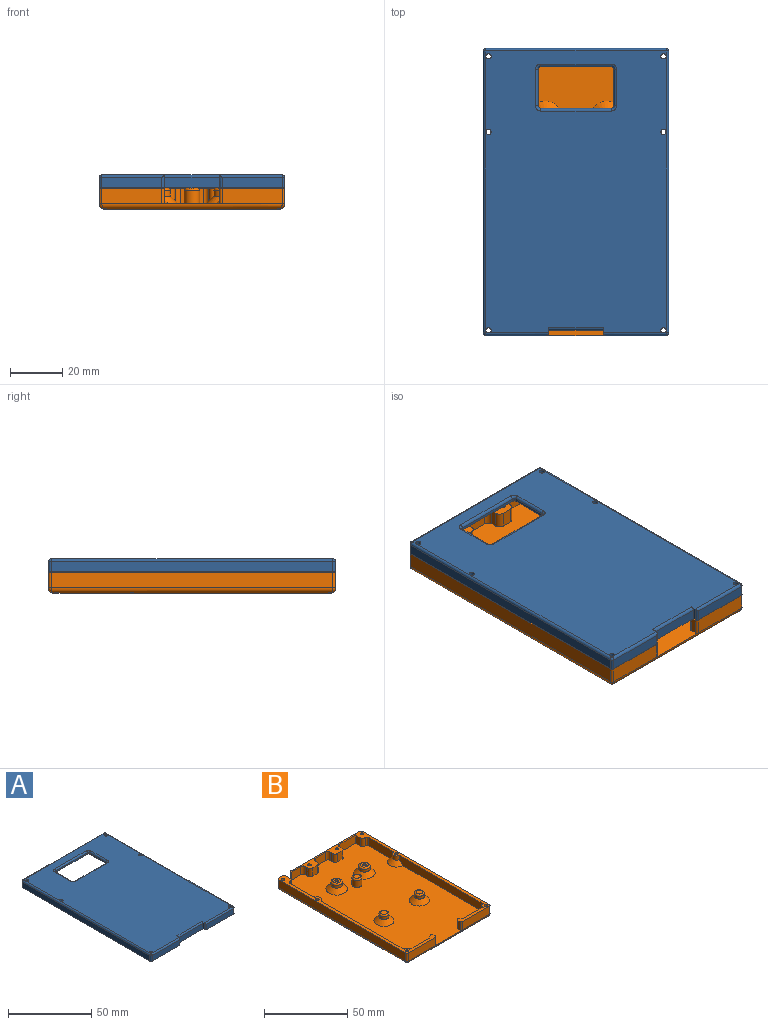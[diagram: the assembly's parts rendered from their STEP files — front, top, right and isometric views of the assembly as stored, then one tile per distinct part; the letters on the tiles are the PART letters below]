
ASSEMBLY  parts=2 mates=1
PART A: 99 faces, bbox 71x110x5 mm
  f0: plane 4x3.68mm, normal (0,1,0), area 14.7mm2, adj f49,f76,f80,f81
  f1: plane 108x69mm, normal (0,0,1), area 6836.2mm2, adj f5,f7,f15,f16,f17,f18,f19,f22
  f2: plane 1x1mm, normal (0,0,1), area 0.2mm2, adj f15,f68,f74
  f3: plane 1x1mm, normal (0,0,1), area 0.2mm2, adj f16,f69,f75
  f4: plane 107x67mm, normal (0,0,-1), area 6312.3mm2, adj f12,f13,f14,f21,f23,f24,f25,f26
  f5: plane 5x2mm, normal (1,0,0), area 5.2mm2, adj f1,f6,f49,f66,f94
  f6: plane 21x4mm, normal (0,-1,0), area 84mm2, adj f5,f7,f49,f94
  f7: plane 5x2mm, normal (-1,0,0), area 5.2mm2, adj f1,f6,f49,f65,f94
  f8: plane 23x4mm, normal (0,-1,0), area 92mm2, adj f49,f65,f67,f68
  f9: plane 108x4mm, normal (1,0,0), area 432mm2, adj f49,f67,f73,f74
  f10: plane 58.32x4mm, normal (0,1,0), area 233.3mm2, adj f49,f73,f79,f80
  f11: plane 108x4mm, normal (-1,0,0), area 432mm2, adj f49,f70,f75,f76
  f12: plane 27x1mm, normal (0,1,0), area 27mm2, adj f4,f52,f53,f54
  f13: plane 14x1mm, normal (1,0,0), area 14mm2, adj f4,f52,f57,f58
  f14: plane 27x1mm, normal (0,-1,0), area 27mm2, adj f4,f57,f60,f63
  f15: cylinder r=1mm len=5mm, axis (0,0,-1), area 31.4mm2, adj f1,f2,f49
  f16: cylinder r=1mm len=5mm, axis (0,0,-1), area 31.4mm2, adj f1,f3,f49
  f17: cylinder r=1mm len=5mm, axis (0,0,-1), area 31.4mm2, adj f1,f49
  f18: cylinder r=1mm len=5mm, axis (0,0,-1), area 31.4mm2, adj f1,f49
  f19: cylinder r=1mm len=5mm, axis (0,0,-1), area 31.4mm2, adj f1,f49
  f20: plane 23x4mm, normal (0,-1,0), area 92mm2, adj f49,f66,f69,f70
  f21: plane 14x1mm, normal (-1,0,0), area 14mm2, adj f4,f54,f59,f60
  f22: cylinder r=1mm len=5mm, axis (0,0,-1), area 31.4mm2, adj f1,f49
  f23: plane 53.71x3mm, normal (0,-1,0), area 161.1mm2, adj f4,f49,f79,f92
  f24: plane 4x3mm, normal (-1,0,0), area 12mm2, adj f4,f49,f92,f93
  f25: plane 3x2.61mm, normal (0,-1,0), area 7.8mm2, adj f4,f26,f49,f93
  f26: plane 22.5x3mm, normal (-1,0,0), area 65.5mm2, adj f4,f25,f27,f49,f96
  f27: cylinder r=2.5mm len=5mm, axis (0,0,1), area 7.9mm2, adj f26,f28,f49,f96
  f28: plane 33x3mm, normal (-1,0,0), area 97mm2, adj f4,f27,f49,f84,f96
  f29: plane 14.38x3mm, normal (0,1,0), area 43.1mm2, adj f4,f49,f84,f85
  f30: cylinder r=3mm len=6mm, axis (0,0,1), area 44.4mm2, adj f4,f49,f85,f86
  f31: plane 14.38x3mm, normal (0,-1,0), area 43.1mm2, adj f4,f49,f86,f87
  f32: plane 33x3mm, normal (-1,0,0), area 97mm2, adj f4,f33,f49,f87,f98
  f33: cylinder r=2.5mm len=2.5mm, axis (0,0,1), area 3.9mm2, adj f32,f34,f49,f98
  f34: plane 16.5x3mm, normal (0,1,0), area 47.5mm2, adj f4,f33,f35,f49,f98
  f35: plane 3.73x3mm, normal (0.6,0.8,0), area 14mm2, adj f4,f34,f49,f82
  f36: plane 20.33x3mm, normal (0,1,0), area 61mm2, adj f4,f49,f82,f83
  f37: plane 3.73x3mm, normal (-0.6,0.8,0), area 14mm2, adj f4,f38,f49,f83
  f38: plane 16.5x3mm, normal (0,1,0), area 47.5mm2, adj f4,f37,f39,f49,f97
  f39: cylinder r=2.5mm len=2.5mm, axis (0,0,1), area 3.9mm2, adj f38,f40,f49,f97
  f40: plane 33x3mm, normal (1,0,0), area 97mm2, adj f4,f39,f49,f91,f97
  f41: plane 14.38x3mm, normal (0,-1,0), area 43.1mm2, adj f4,f49,f88,f91
  f42: cylinder r=3mm len=6mm, axis (0,0,1), area 44.4mm2, adj f4,f49,f88,f89
  f43: plane 14.38x3mm, normal (0,1,0), area 43.1mm2, adj f4,f49,f89,f90
  f44: plane 33x3mm, normal (1,0,0), area 97mm2, adj f4,f45,f49,f90,f95
  f45: cylinder r=2.5mm len=5mm, axis (0,0,1), area 7.9mm2, adj f44,f46,f49,f95
  f46: plane 22.5x3mm, normal (1,0,0), area 65.5mm2, adj f4,f45,f47,f49,f95
  f47: plane 3x2.68mm, normal (0,-1,0), area 8mm2, adj f4,f46,f49,f64
  f48: plane 5x3mm, normal (1,0,0), area 15mm2, adj f4,f49,f64,f81
  f49: plane 110x71mm, normal (0,0,-1), area 872.7mm2, adj f0,f5,f6,f7,f8,f9,f10,f11
  f50: cylinder r=3mm len=6mm, axis (0,0,1), area 56.5mm2, adj f4,f51
  f51: plane 6x6mm, normal (0,0,-1), area 28.3mm2, adj f50
  f52: cylinder r=1mm len=1mm, axis (0,0,1), area 1.6mm2, adj f4,f12,f13,f55
  f53: cylinder r=1mm len=27mm, axis (1,0,0), area 42.4mm2, adj f1,f12,f55,f56
  f54: cylinder r=1mm len=1mm, axis (0,0,-1), area 1.6mm2, adj f4,f12,f21,f56
  f55: torus R=2mm, axis (0,0,1), area 3.4mm2, adj f1,f52,f53,f58
  f56: torus R=2mm, axis (0,0,1), area 3.4mm2, adj f1,f53,f54,f59
  f57: cylinder r=1mm len=1mm, axis (0,0,-1), area 1.6mm2, adj f4,f13,f14,f61
  f58: cylinder r=1mm len=14mm, axis (0,-1,0), area 22mm2, adj f1,f13,f55,f61
  f59: cylinder r=1mm len=14mm, axis (0,1,0), area 22mm2, adj f1,f21,f56,f62
  f60: cylinder r=1mm len=1mm, axis (0,0,1), area 1.6mm2, adj f4,f14,f21,f62
  f61: torus R=2mm, axis (0,0,1), area 3.4mm2, adj f1,f57,f58,f63
  f62: torus R=2mm, axis (0,0,1), area 3.4mm2, adj f1,f59,f60,f63
  f63: cylinder r=1mm len=27mm, axis (-1,0,0), area 42.4mm2, adj f1,f14,f61,f62
  f64: cylinder r=1mm len=3mm, axis (0,0,1), area 4.7mm2, adj f4,f47,f48,f49
  f65: cylinder r=1mm len=5mm, axis (0,0,1), area 7.3mm2, adj f7,f8,f49,f68
  f66: cylinder r=1mm len=5mm, axis (0,0,-1), area 7.3mm2, adj f5,f20,f49,f69
  f67: cylinder r=1mm len=4mm, axis (0,0,1), area 6.3mm2, adj f8,f9,f49,f71
  f68: cylinder r=1mm len=24mm, axis (-1,0,0), area 37.1mm2, adj f1,f2,f8,f65,f71
  f69: cylinder r=1mm len=24mm, axis (-1,0,0), area 37.1mm2, adj f1,f3,f20,f66,f72
  f70: cylinder r=1mm len=4mm, axis (0,0,-1), area 6.3mm2, adj f11,f20,f49,f72
  f71: sphere r=1mm, area 1.6mm2, adj f67,f68,f74
  f72: sphere r=1mm, area 1.6mm2, adj f69,f70,f75
  f73: cylinder r=1mm len=4mm, axis (0,0,1), area 6.3mm2, adj f9,f10,f49,f77
  f74: cylinder r=1mm len=108mm, axis (0,-1,0), area 169.6mm2, adj f1,f2,f9,f71,f77
  f75: cylinder r=1mm len=108mm, axis (0,1,0), area 169.6mm2, adj f1,f3,f11,f72,f78
  f76: cylinder r=1mm len=4mm, axis (0,0,-1), area 6.3mm2, adj f0,f11,f49,f78
  f77: sphere r=1mm, area 1.6mm2, adj f73,f74,f80
  f78: sphere r=1mm, area 1.6mm2, adj f75,f76,f80
  f79: cylinder r=1mm len=4mm, axis (0,0,-1), area 5.3mm2, adj f10,f23,f49,f80
  f80: cylinder r=1mm len=69mm, axis (1,0,0), area 117.4mm2, adj f0,f1,f4,f10,f77,f78,f79,f81
  f81: cylinder r=1mm len=4mm, axis (0,0,1), area 5.3mm2, adj f0,f48,f49,f80
  f82: cylinder r=1mm len=3mm, axis (0,0,1), area 1.9mm2, adj f4,f35,f36,f49
  f83: cylinder r=1mm len=3mm, axis (0,0,-1), area 1.9mm2, adj f4,f36,f37,f49
  f84: cylinder r=1mm len=3mm, axis (0,0,-1), area 4.7mm2, adj f4,f28,f29,f49
  f85: cylinder r=1mm len=3mm, axis (0,0,1), area 2.7mm2, adj f4,f29,f30,f49
  f86: cylinder r=1mm len=3mm, axis (0,0,1), area 2.7mm2, adj f4,f30,f31,f49
  f87: cylinder r=1mm len=3mm, axis (0,0,1), area 4.7mm2, adj f4,f31,f32,f49
  f88: cylinder r=1mm len=3mm, axis (0,0,1), area 2.7mm2, adj f4,f41,f42,f49
  f89: cylinder r=1mm len=3mm, axis (0,0,1), area 2.7mm2, adj f4,f42,f43,f49
  f90: cylinder r=1mm len=3mm, axis (0,0,1), area 4.7mm2, adj f4,f43,f44,f49
  f91: cylinder r=1mm len=3mm, axis (0,0,-1), area 4.7mm2, adj f4,f40,f41,f49
  f92: cylinder r=1mm len=3mm, axis (0,0,1), area 4.7mm2, adj f4,f23,f24,f49
  f93: cylinder r=1mm len=3mm, axis (0,0,1), area 4.7mm2, adj f4,f24,f25,f49
  f94: cylinder r=1mm len=21mm, axis (-1,0,0), area 33mm2, adj f1,f5,f6,f7
  f95: cone r=4.5mm half-angle=45deg, axis (0,0,1), area 31.1mm2, adj f4,f44,f45,f46
  f96: cone r=4.5mm half-angle=45deg, axis (0,0,1), area 31.1mm2, adj f4,f26,f27,f28
  f97: cone r=4.5mm half-angle=45deg, axis (0,0,1), area 15.6mm2, adj f4,f38,f39,f40
  f98: cone r=4.5mm half-angle=45deg, axis (0,0,1), area 15.6mm2, adj f4,f32,f33,f34
PART B: 105 faces, bbox 71x110x8 mm
  f0: plane 23x6mm, normal (0,-1,0), area 138mm2, adj f3,f74,f85,f92
  f1: plane 57.32x6mm, normal (0,1,0), area 343.9mm2, adj f2,f75,f78,f81
  f2: plane 110x60.32mm, normal (0,0,1), area 443.3mm2, adj f1,f4,f5,f7,f9,f12,f22,f23
  f3: plane 110x25mm, normal (0,0,1), area 302.7mm2, adj f0,f6,f8,f10,f11,f13,f15,f16
  f4: plane 23x6mm, normal (0,-1,0), area 138mm2, adj f2,f74,f89,f91
  f5: plane 107x6mm, normal (1,0,0), area 642mm2, adj f2,f76,f78,f89
  f6: plane 6x3.68mm, normal (0,1,0), area 22.1mm2, adj f3,f75,f82,f87
  f7: cylinder r=1mm len=8mm, axis (0,0,1), area 49.8mm2, adj f2,f14,f76
  f8: cylinder r=1mm len=8mm, axis (0,0,1), area 50.3mm2, adj f3,f14,f73
  f9: cylinder r=1mm len=8mm, axis (0,0,1), area 49.8mm2, adj f2,f14,f76
  f10: cylinder r=1mm len=8mm, axis (0,0,1), area 50.3mm2, adj f3,f14,f73
  f11: plane 108x6mm, normal (-1,0,0), area 648mm2, adj f3,f73,f85,f87
  f12: cylinder r=1mm len=8mm, axis (0,0,1), area 49.6mm2, adj f2,f14,f74,f76,f90
  f13: cylinder r=1mm len=8mm, axis (0,0,1), area 49.7mm2, adj f3,f14,f73,f74,f86
  f14: plane 106x67mm, normal (0,0,-1), area 7094.1mm2, adj f7,f8,f9,f10,f12,f13,f73,f74
  f15: plane 18.97x6mm, normal (1,0,0), area 113.8mm2, adj f3,f47,f61,f69
  f16: cylinder r=2.5mm len=6mm, axis (0,0,1), area 33.3mm2, adj f3,f47,f61,f62
  f17: plane 69.47x6mm, normal (1,0,0), area 412.3mm2, adj f3,f18,f47,f62,f99
  f18: cylinder r=2.5mm len=3mm, axis (0,0,1), area 11.8mm2, adj f3,f17,f19,f99
  f19: plane 16.5x6mm, normal (0,1,0), area 94.5mm2, adj f3,f18,f20,f47,f99
  f20: plane 6x2.4mm, normal (-0.6,0.8,0), area 18mm2, adj f3,f19,f47,f84
  f21: plane 6x2mm, normal (1,0,0), area 12mm2, adj f3,f47,f84,f92
  f22: plane 6x2mm, normal (-1,0,0), area 12mm2, adj f2,f47,f80,f91
  f23: plane 6x2.4mm, normal (0.6,0.8,0), area 18mm2, adj f2,f24,f47,f80
  f24: plane 16.5x6mm, normal (0,1,0), area 94.5mm2, adj f2,f23,f25,f47,f98
  f25: cylinder r=2.5mm len=3mm, axis (0,0,1), area 11.8mm2, adj f2,f24,f26,f98
  f26: plane 71x6mm, normal (-1,0,0), area 417mm2, adj f2,f25,f27,f47,f98,f100
  f27: cylinder r=2.5mm len=5mm, axis (0,0,1), area 23.6mm2, adj f2,f26,f28,f100
  f28: plane 21.5x6mm, normal (-1,0,0), area 124.5mm2, adj f2,f27,f47,f79,f100
  f29: plane 6x0.61mm, normal (0,-1,0), area 3.6mm2, adj f2,f47,f65,f79
  f30: plane 6x4mm, normal (-1,0,0), area 24mm2, adj f2,f31,f47,f65
  f31: plane 13.39x6mm, normal (0,-1,0), area 80.4mm2, adj f2,f30,f47,f63
  f32: plane 6x2mm, normal (1,0,0), area 12mm2, adj f2,f47,f63,f66
  f33: plane 6x4mm, normal (0,-1,0), area 24mm2, adj f2,f47,f66,f67
  f34: plane 6x2mm, normal (-1,0,0), area 12mm2, adj f2,f47,f67,f71
  f35: plane 9x6mm, normal (0,-1,0), area 54mm2, adj f2,f47,f71,f72
  f36: plane 6x2mm, normal (1,0,0), area 12mm2, adj f2,f47,f68,f72
  f37: plane 6x4mm, normal (0,-1,0), area 24mm2, adj f2,f47,f68,f70
  f38: plane 6x2mm, normal (-1,0,0), area 12mm2, adj f2,f47,f64,f70
  f39: plane 8.32x6mm, normal (0,-1,0), area 49.9mm2, adj f2,f47,f64,f81
  f40: plane 6x5mm, normal (1,0,0), area 30mm2, adj f3,f47,f82,f83
  f41: cylinder r=3mm len=6mm, axis (0,0,1), area 37.7mm2, adj f93,f102
  f42: cylinder r=3.4mm len=6.8mm, axis (0,0,1), area 42.7mm2, adj f95,f104
  f43: cylinder r=3.4mm len=6.8mm, axis (0,0,1), area 42.7mm2, adj f97,f103
  f44: cylinder r=3mm len=6mm, axis (0,0,1), area 94.2mm2, adj f47,f96
  f45: plane 6x0.68mm, normal (0,-1,0), area 4.1mm2, adj f3,f47,f69,f83
  f46: cylinder r=3mm len=6mm, axis (0,0,1), area 37.7mm2, adj f94,f101
  f47: plane 110x67mm, normal (0,0,1), area 6449.5mm2, adj f15,f16,f17,f19,f20,f21,f22,f23
  f48: plane 4x4mm, normal (0,0,1), area 12.6mm2, adj f96
  f49: plane 4.8x4.8mm, normal (0,0,1), area 14.6mm2, adj f55,f95
  f50: plane 4x4mm, normal (0,0,1), area 12.6mm2, adj f93
  f51: cylinder r=1.05mm len=6mm, axis (0,0,1), area 39.6mm2, adj f2,f52
  f52: plane 2.1x2.1mm, normal (0,0,1), area 3.5mm2, adj f51
  f53: cylinder r=1.05mm len=6mm, axis (0,0,1), area 39.6mm2, adj f2,f54
  f54: plane 2.1x2.1mm, normal (0,0,1), area 3.5mm2, adj f53
  f55: cylinder r=1.05mm len=6mm, axis (0,0,1), area 39.6mm2, adj f49,f56
  f56: plane 2.1x2.1mm, normal (0,0,1), area 3.5mm2, adj f55
  f57: plane 4.8x4.8mm, normal (0,0,1), area 14.6mm2, adj f58,f97
  f58: cylinder r=1.05mm len=6mm, axis (0,0,1), area 39.6mm2, adj f57,f59
  f59: plane 2.1x2.1mm, normal (0,0,1), area 3.5mm2, adj f58
  f60: plane 4x4mm, normal (0,0,1), area 12.6mm2, adj f94
  f61: cylinder r=2mm len=6mm, axis (0,0,1), area 13.3mm2, adj f3,f15,f16,f47
  f62: cylinder r=2mm len=6mm, axis (0,0,1), area 13.3mm2, adj f3,f16,f17,f47
  f63: cylinder r=2mm len=6mm, axis (0,0,-1), area 18.8mm2, adj f2,f31,f32,f47
  f64: cylinder r=2mm len=6mm, axis (0,0,-1), area 18.8mm2, adj f2,f38,f39,f47
  f65: cylinder r=2mm len=6mm, axis (0,0,1), area 18.8mm2, adj f2,f29,f30,f47
  f66: cylinder r=2mm len=6mm, axis (0,0,1), area 18.8mm2, adj f2,f32,f33,f47
  f67: cylinder r=2mm len=6mm, axis (0,0,1), area 18.8mm2, adj f2,f33,f34,f47
  f68: cylinder r=2mm len=6mm, axis (0,0,-1), area 18.8mm2, adj f2,f36,f37,f47
  f69: cylinder r=2mm len=6mm, axis (0,0,-1), area 18.8mm2, adj f3,f15,f45,f47
  f70: cylinder r=2mm len=6mm, axis (0,0,-1), area 18.8mm2, adj f2,f37,f38,f47
  f71: cylinder r=2mm len=6mm, axis (0,0,-1), area 18.8mm2, adj f2,f34,f35,f47
  f72: cylinder r=2mm len=6mm, axis (0,0,1), area 18.8mm2, adj f2,f35,f36,f47
  f73: cylinder r=2mm len=108mm, axis (0,1,0), area 332.7mm2, adj f8,f10,f11,f13,f14,f86,f88
  f74: cylinder r=2mm len=69mm, axis (-1,0,0), area 212mm2, adj f0,f4,f12,f13,f14,f47,f86,f90
  f75: cylinder r=2mm len=68mm, axis (1,0,0), area 212.1mm2, adj f1,f6,f14,f47,f77,f88
  f76: cylinder r=2mm len=107mm, axis (0,-1,0), area 330.7mm2, adj f5,f7,f9,f12,f14,f77,f90
  f77: sphere r=2mm, area 4mm2, adj f75,f76,f78
  f78: cylinder r=2mm len=6mm, axis (0,0,-1), area 18.8mm2, adj f1,f2,f5,f77
  f79: cylinder r=1mm len=6mm, axis (0,0,1), area 9.4mm2, adj f2,f28,f29,f47
  f80: cylinder r=1mm len=6mm, axis (0,0,-1), area 13.3mm2, adj f2,f22,f23,f47
  f81: cylinder r=1mm len=6mm, axis (0,0,1), area 9.4mm2, adj f1,f2,f39,f47
  f82: cylinder r=1mm len=6mm, axis (0,0,-1), area 9.4mm2, adj f3,f6,f40,f47
  f83: cylinder r=1mm len=6mm, axis (0,0,1), area 9.4mm2, adj f3,f40,f45,f47
  f84: cylinder r=1mm len=6mm, axis (0,0,-1), area 13.3mm2, adj f3,f20,f21,f47
  f85: cylinder r=1mm len=6mm, axis (0,0,1), area 9.4mm2, adj f0,f3,f11,f86
  f86: bspline ~2.32x1.65mm, area 3mm2, adj f13,f73,f74,f85
  f87: cylinder r=1mm len=6mm, axis (0,0,1), area 9.4mm2, adj f3,f6,f11,f88
  f88: bspline ~2.1x2mm, area 2.2mm2, adj f73,f75,f87
  f89: cylinder r=1mm len=6mm, axis (0,0,-1), area 9.4mm2, adj f2,f4,f5,f90
  f90: bspline ~2.32x1.65mm, area 3mm2, adj f12,f74,f76,f89
  f91: cylinder r=1mm len=6mm, axis (0,0,-1), area 9.4mm2, adj f2,f4,f22,f47
  f92: cylinder r=1mm len=6mm, axis (0,0,1), area 9.4mm2, adj f0,f3,f21,f47
  f93: torus R=2mm, axis (0,0,1), area 26mm2, adj f41,f50
  f94: torus R=2mm, axis (0,0,1), area 26mm2, adj f46,f60
  f95: torus R=2.4mm, axis (0,0,1), area 30mm2, adj f42,f49
  f96: torus R=2mm, axis (0,0,1), area 26mm2, adj f44,f48
  f97: torus R=2.4mm, axis (0,0,1), area 30mm2, adj f43,f57
  f98: cone r=2.5mm half-angle=45deg, axis (0,0,-1), area 26.7mm2, adj f24,f25,f26,f47
  f99: cone r=2.5mm half-angle=45deg, axis (0,0,-1), area 26.7mm2, adj f17,f18,f19,f47
  f100: cone r=2.5mm half-angle=45deg, axis (0,0,-1), area 53.3mm2, adj f26,f27,f28,f47
  f101: cone r=3mm half-angle=45deg, axis (0,0,-1), area 120mm2, adj f46,f47
  f102: cone r=3mm half-angle=45deg, axis (0,0,-1), area 120mm2, adj f41,f47
  f103: cone r=3.4mm half-angle=45deg, axis (0,0,-1), area 130.6mm2, adj f43,f47
  f104: cone r=3.4mm half-angle=45deg, axis (0,0,-1), area 130.6mm2, adj f42,f47
PLACE A t=(29.99,-13.69,16.56)mm
PLACE B t=(29.99,-13.69,13.46)mm
MATE slider B.f10 <-> A.f19  axis (0,0,1) through (-3.51,53.25,13.46)mm
